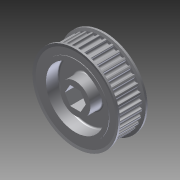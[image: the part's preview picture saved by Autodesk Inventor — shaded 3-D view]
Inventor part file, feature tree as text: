
AUTODESK INVENTOR PART (.ipt)
format: ipt  version: 2014 SP1 (Build 180222100, 222)  size: 1,035,264 bytes
history: native  units: in
note: dims shown in document units (in); Inventor stores cm internally (conversion verified against a paired STEP export)
features: mirror x1, other x1, imported_body x1
ambient origin geometry x8: Origin, YZ Plane, XZ Plane, XY Plane, X Axis, Y Axis, Z Axis, Center Point
bodies: Body1 (feature_tree)
feature tree (3):
  mirror  "Mirror1"
  other  "217-3232-STEP1"
  imported_body  "Base1"
